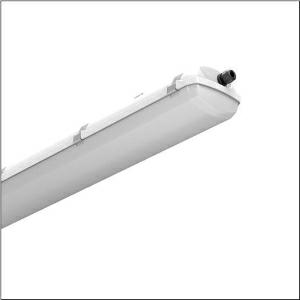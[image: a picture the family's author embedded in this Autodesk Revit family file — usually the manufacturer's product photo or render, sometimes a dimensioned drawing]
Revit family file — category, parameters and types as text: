
# Revit family: monsun_ex_51fxa27l440a
name_source: partatom
category: Lighting Fixtures
units: mm (PartAtom-declared; Revit-internal decimal feet)

## family parameters
Cut with Voids When Loaded = No
Host = Face
Light Source = No
Part Type = Normal
Room Calculation Point = No
Round Connector Dimension = Use Diameter
Shared = No

## types (1)
- Monsun Ex (1 x LED, 4650 lm, 33 W, 4000K)
    Apparent Load = 33 VA
    CIE Flux Codes = 46 76 94 98 100
    Color Rendering = 80
    Color Temperature = 4000K
    Default Elevation = 1800 mm
    Description = Monsun Ex, damp-proof luminaire, primary optical cover: cover, of PC, UV-stabilised, opal, light emission: direct distribution, primary light characteristic: symmetric, installation type: surface-mounted, LED, rated luminous flux: 4.650lm, luminous efficacy: 141lm/W, light colour: 840, colour temperature: 4000K, control gear: ON/OFF, with terminal, 3-pole, max. 2.5mm², through-wiring: 5x 2.5mm², mains connection: 220..250V, AC, 50/60Hz, rated input power: 33W, housing, of PC, light grey (RAL 7035), incl. 2x Ex cable gland M20 for cable diameter 7..12mm with sealing, incl. 1x Ex locking screw M20 with sealing, length: 1.280mm, width: 155mm, height: 105mm, clip for enclosure, of stainless steel, protection rating (complete): IP66, insulation class (complete): insulation class I (protective earthing), certification: CE, explosion class: zone 1,21 II 2G Ex eb mb op is IIC T4 Gb, II 2D Ex tb op is IIIC T67°C Db, impact resistance: IK10, permissible operating ambient temperature: -20..+40°C, contact your sales advisor before using the luminaires in applications with unclear chemical exposure, large temperature fluctuations or condensation-forming humidity, packaging unit: 1 piece
    Height = 105 mm
    Lamp = 1 x LED
    Lamp Light Flux = 4650 lm
    Lamp Power = 33 W
    Lamp count = 1
    Length = 1280 mm
    Luminous efficacy = 141 lm/W
    Manufacturer = Siteco
    ModVariant = No
    Model = 51FXA27L440A
    Mounting Place = Ceiling
    Mounting Type = Surface mounted
    Number of Poles = 1
    OnlyDefault = Yes
    Power Factor = 1
    Product Name = Monsun Ex
    Product group = damp-proof luminaire
    ProductGroupID = 300
    Protection Class = Protection class I
    Protection Degree = IP 66
    RLX_Detail_Level = 1
    RLX_Emergency_Light_Flux = 0 lm
    RLX_Emergency_Type = 0
    RLX_Emergency_Type_DB = No
    RlxData = <blob elided: 41717 chars, md5=b219ba69>
    Socket = socket
    Standby Power = 0 W
    System Light Flux = 4650 lm
    System Power = 33 W
    Type Comments = Product without accessories
    Type Image = l_1258882.jpg
    URL = http://relux.com
    VarID = ---
    Voltage = 0 V
    Weight = 0.00 kg
    Width = 155 mm

## geometry (parser evidence)
native form markers: Blend x4, Sweep x10
no freeform markers — native parametric forms only
